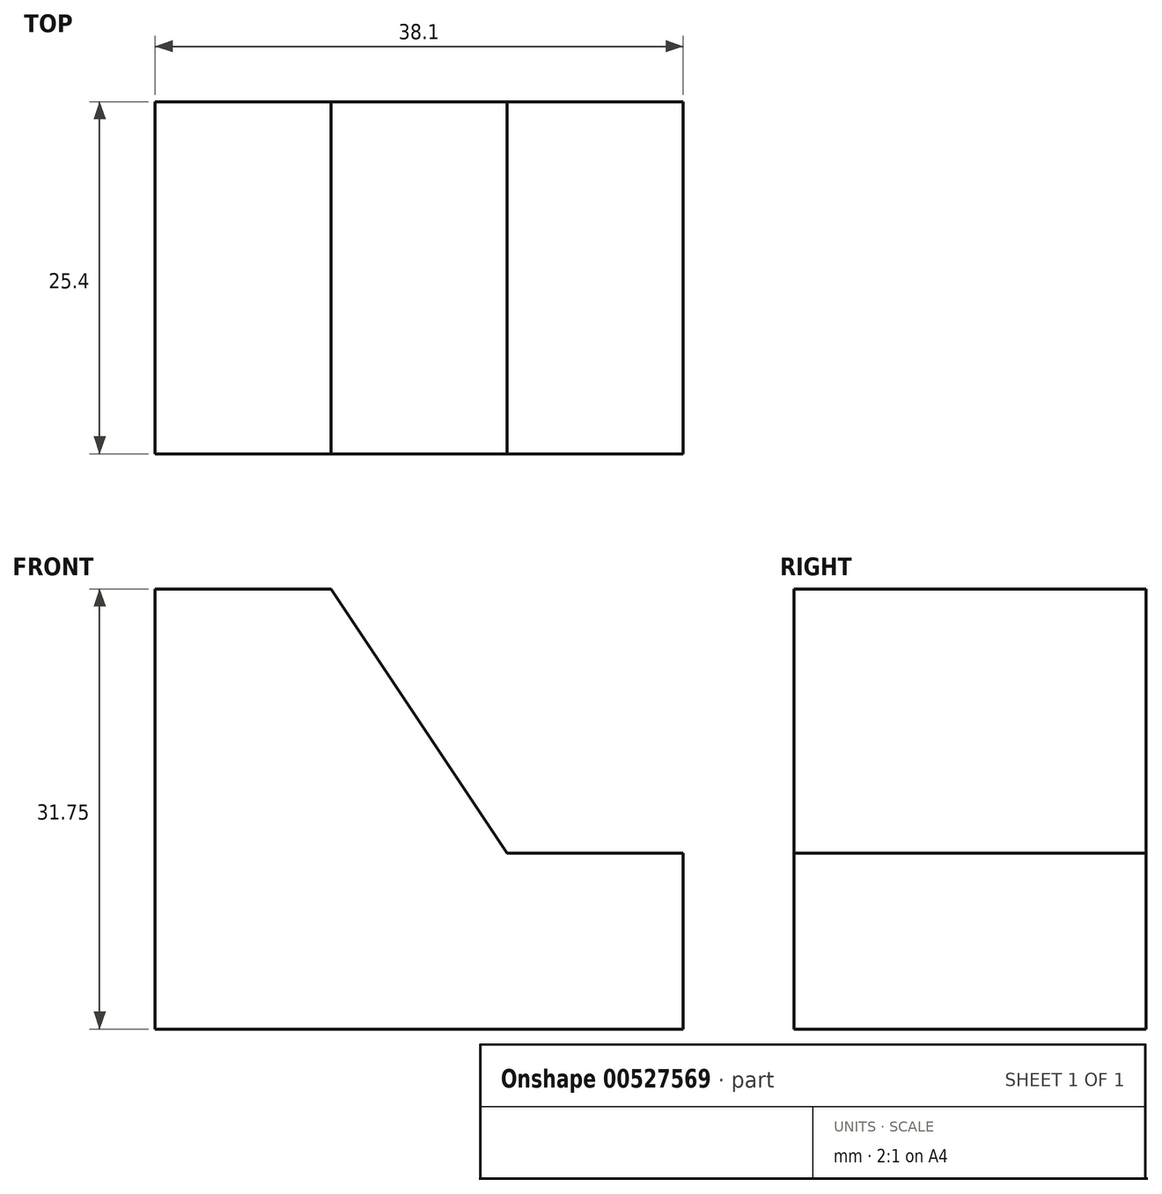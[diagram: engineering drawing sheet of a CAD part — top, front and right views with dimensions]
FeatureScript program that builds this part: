
annotation { "Feature Type Name" : "Feature", "Feature Type Description" : "" }
export const myFeature = defineFeature(function(context is Context, id is Id, definition is map)
    precondition{}
    {
        {
            var Q0;
            Q0=qCreatedBy(makeId("Front.planeOp"),FACE);
            var sketch = newSketch(context, id + "F0", { "sketchPlane" : qUnion([Q0])});
            skLineSegment(sketch, "E0", {"start": v(0, 0) * mm, "end": v(38.1, 0) * mm});
            skLineSegment(sketch, "E1", {"start": v(38.1, 0) * mm, "end": v(38.1, 12.7) * mm});
            skLineSegment(sketch, "E2", {"start": v(38.1, 12.7) * mm, "end": v(25.4, 12.7) * mm});
            skLineSegment(sketch, "E3", {"start": v(25.4, 12.7) * mm, "end": v(25.4, 31.75) * mm});
            skLineSegment(sketch, "E4", {"start": v(25.4, 31.75) * mm, "end": v(0, 31.75) * mm});
            skLineSegment(sketch, "E5", {"start": v(0, 31.75) * mm, "end": v(0, 0) * mm});
            skSolve(sketch);
        }
        {
            var Q0;
            Q0=makeQuery(id+"F0.imprint","IMPRINT",FACE,{"disambiguationData":[TD([[makeQuery(id+"F0.imprint","IMPRINT",EDGE,{"derivedFrom":sQuery(id+"F0.wireOp",EDGE,"E0")}),1.0]])]});
            extrude(context, id + "F1", {"entities" : qUnion([Q0]), "depth" : 25.4 * mm, "offsetDistance" : 25.4 * mm});
        }
        {
            var Q0;
            Q0=makeQuery(id+"F1.opExtrude","CAP_FACE",FACE,{"disambiguationData":[OSD([sQuery(id+"F0.wireOp",EDGE,"E0"),sQuery(id+"F0.wireOp",EDGE,"E1"),sQuery(id+"F0.wireOp",EDGE,"E2"),sQuery(id+"F0.wireOp",EDGE,"E3"),sQuery(id+"F0.wireOp",EDGE,"E4"),sQuery(id+"F0.wireOp",EDGE,"E5")])],"isStart":false});
            var sketch = newSketch(context, id + "F2", { "sketchPlane" : qUnion([Q0])});
            skLineSegment(sketch, "E6", {"start": v(25.4, 12.7) * mm, "end": v(12.7, 31.75) * mm});
            skSolve(sketch);
        }
        {
            var Q0;
            {var subQ0=sQuery(id+"F2.wireOp",EDGE,"E6");Q0=makeQuery(id+"F2.imprint","IMPRINT",FACE,{"disambiguationData":[TD([[makeQuery(id+"F2.imprint","IMPRINT",EDGE,{"derivedFrom":subQ0}),-1.0]])]});}
            extrude(context, id + "F3", {"entities" : qUnion([Q0]), "operationType" : NewBodyOperationType.REMOVE, "oppositeDirection" : true, "depth" : 25.4 * mm, "offsetDistance" : 25.4 * mm});
        }
    });
